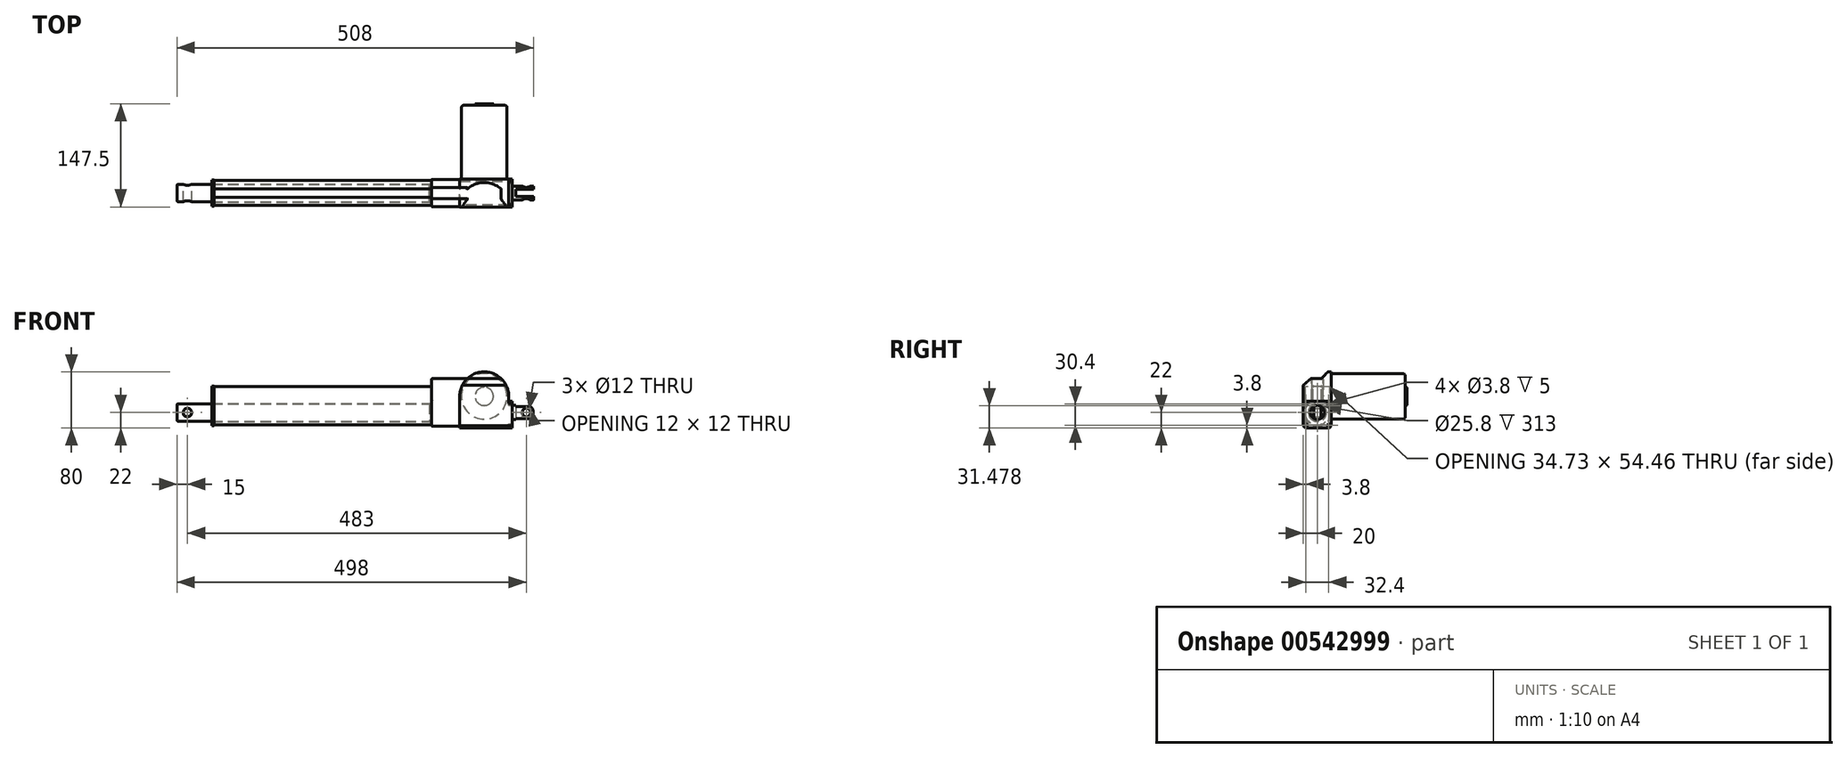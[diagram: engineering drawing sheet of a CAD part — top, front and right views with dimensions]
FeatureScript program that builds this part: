
annotation { "Feature Type Name" : "Feature", "Feature Type Description" : "" }
export const myFeature = defineFeature(function(context is Context, id is Id, definition is map)
    precondition{}
    {
        {
            var Q0;
            Q0=qCreatedBy(makeId("Right.planeOp"),FACE);
            var sketch = newSketch(context, id + "F0", { "sketchPlane" : qUnion([Q0])});
            skCircle(sketch, "E0", {"center": v(0, 0) * mm, "radius": 10 * mm});
            skSolve(sketch);
        }
        {
            var Q0;
            Q0 = qSketchRegion(id + "F0", true);
            var Q1;
            Q1 = qSketchRegion(id + "F2", true);
            extrude(context, id + "F1", {"entities" : qUnion([Q0, Q1]), "depth" : 30 * mm, "offsetDistance" : 25.4 * mm});
        }
        {
            var Q0;
            Q0=qCreatedBy(makeId("Front.planeOp"),FACE);
            var sketch = newSketch(context, id + "F2", { "sketchPlane" : qUnion([Q0])});
            skPoint(sketch, "E1", {"position": v(20, 0) * mm});
            skLineSegment(sketch, "E2", {"start": v(20, -26.83) * mm, "end": v(20, 0) * mm, "construction": true});
            skLineSegment(sketch, "E3", {"start": v(20, 0) * mm, "end": v(20, 12.82) * mm, "construction": true});
            skLineSegment(sketch, "E4", {"start": v(20, 10) * mm, "end": v(30, 10) * mm});
            skLineSegment(sketch, "E5.0", {"start": v(30, 10) * mm, "end": v(30, -10) * mm});
            skLineSegment(sketch, "E6", {"start": v(30, -10) * mm, "end": v(20, -10) * mm});
            skArc(sketch, "E7", {"start": v(20, 10) * mm, "mid": v(30, 0) * mm, "end": v(20, -10) * mm});
            skSolve(sketch);
        }
        {
            var Q0;
            Q0 = qSketchRegion(id + "F2", true);
            extrude(context, id + "F3", {"entities" : qUnion([Q0]), "operationType" : NewBodyOperationType.REMOVE, "oppositeDirection" : true, "depth" : 20 * mm, "offsetDistance" : 25 * mm, "symmetric" : true});
        }
        {
            var Q0;
            Q0=qCreatedBy(makeId("Front.planeOp"),FACE);
            cPlane(context, id + "F4", {"entities" : qUnion([Q0]), "cplaneType" : CPlaneType.OFFSET, "offset" : 20 * mm, "oppositeDirection" : true, "width" : 150 * mm, "height" : 150 * mm});
        }
        {
            var Q0;
            Q0=qCreatedBy(id+"F4.planeOp",FACE);
            var sketch = newSketch(context, id + "F5", { "sketchPlane" : qUnion([Q0])});
            skLineSegment(sketch, "E8", {"start": v(0, 0) * mm, "end": v(20, 0) * mm, "construction": true});
            skCircle(sketch, "E9", {"center": v(20, 0) * mm, "radius": 6 * mm});
            skSolve(sketch);
        }
        {
            var Q0;
            Q0=qCreatedBy(makeId("Right.planeOp"),FACE);
            var sketch = newSketch(context, id + "F6", { "sketchPlane" : qUnion([Q0])});
            skLineSegment(sketch, "E10.bottom", {"start": v(20, 16) * mm, "end": v(-20, 16) * mm});
            skLineSegment(sketch, "E10.top", {"start": v(20, -22) * mm, "end": v(-20, -22) * mm});
            skLineSegment(sketch, "E10.left", {"start": v(20, 16) * mm, "end": v(20, -22) * mm});
            skLineSegment(sketch, "E10.right", {"start": v(-20, 16) * mm, "end": v(-20, -22) * mm});
            skPoint(sketch, "E11.visualSharp", {"position": v(20, 16) * mm});
            skPoint(sketch, "E12.visualSharp", {"position": v(20, -22) * mm});
            skPoint(sketch, "E13.visualSharp", {"position": v(-20, 16) * mm});
            skCircle(sketch, "E14", {"center": v(16.2, 12.2) * mm, "radius": 1.9 * mm});
            skCircle(sketch, "E15", {"center": v(16.2, -18.2) * mm, "radius": 1.9 * mm});
            skCircle(sketch, "E16", {"center": v(-16.2, -18.2) * mm, "radius": 1.9 * mm});
            skCircle(sketch, "E17", {"center": v(-16.2, 12.2) * mm, "radius": 1.9 * mm});
            skSolve(sketch);
        }
        {
            var Q0;
            Q0=makeQuery(id+"F6.imprint","IMPRINT",FACE,{"disambiguationData":[TD([[makeQuery(id+"F6.imprint","IMPRINT",EDGE,{"derivedFrom":sQuery(id+"F6.wireOp",EDGE,"E10.bottom")}),1.0]])]});
            extrude(context, id + "F7", {"entities" : qUnion([Q0]), "operationType" : NewBodyOperationType.ADD, "oppositeDirection" : true, "depth" : 5 * mm, "offsetDistance" : 25 * mm});
        }
        {
            var Q0;
            Q0=qCreatedBy(makeId("Top.planeOp"),FACE);
            cPlane(context, id + "F8", {"entities" : qUnion([Q0]), "cplaneType" : CPlaneType.OFFSET, "offset" : 15 * mm, "oppositeDirection" : true, "width" : 150 * mm, "height" : 150 * mm});
        }
        {
            var Q0;
            Q0=qCreatedBy(id+"F8.planeOp",FACE);
            var sketch = newSketch(context, id + "F9", { "sketchPlane" : qUnion([Q0])});
            skPoint(sketch, "E18.0", {"position": v(30, 0) * mm});
            skLineSegment(sketch, "E19.bottom", {"start": v(30, -5) * mm, "end": v(5, -5) * mm});
            skLineSegment(sketch, "E19.top", {"start": v(30, 5) * mm, "end": v(5, 5) * mm});
            skLineSegment(sketch, "E19.left", {"start": v(30, -5) * mm, "end": v(30, 5) * mm});
            skLineSegment(sketch, "E19.right", {"start": v(5, -5) * mm, "end": v(5, 5) * mm});
            skSolve(sketch);
        }
        {
            var Q0;
            Q0=makeQuery(id+"F9.imprint","IMPRINT",FACE,{"disambiguationData":[TD([[makeQuery(id+"F9.imprint","IMPRINT",EDGE,{"derivedFrom":sQuery(id+"F9.wireOp",EDGE,"E19.bottom")}),-1.0]])]});
            extrude(context, id + "F10", {"entities" : qUnion([Q0]), "operationType" : NewBodyOperationType.REMOVE, "endBound" : BoundingType.THROUGH_ALL, "depth" : 26.4 * mm, "offsetDistance" : 25 * mm});
        }
        {
            var Q0;
            Q0=makeQuery(id+"F7.opExtrude","SWEPT_EDGE",EDGE,{"disambiguationData":[OSD([sQuery(id+"F6.wireOp",EDGE,"E10.top"),sQuery(id+"F6.wireOp",EDGE,"E10.left")])]});
            var Q1;
            Q1=makeQuery(id+"F7.opExtrude","SWEPT_EDGE",EDGE,{"disambiguationData":[OSD([sQuery(id+"F6.wireOp",EDGE,"E10.bottom"),sQuery(id+"F6.wireOp",EDGE,"E10.left")])]});
            var Q2;
            Q2=makeQuery(id+"F7.opExtrude","SWEPT_EDGE",EDGE,{"disambiguationData":[OSD([sQuery(id+"F6.wireOp",EDGE,"E10.bottom"),sQuery(id+"F6.wireOp",EDGE,"E10.right")])]});
            var Q3;
            Q3=makeQuery(id+"F7.opExtrude","SWEPT_EDGE",EDGE,{"disambiguationData":[OSD([sQuery(id+"F6.wireOp",EDGE,"E10.top"),sQuery(id+"F6.wireOp",EDGE,"E10.right")])]});
            chamfer(context, id + "F11", {"entities" : qUnion([Q0, Q1, Q2, Q3]), "width" : 3 * mm, "tangentPropagation" : true});
        }
        {
            var Q0;
            Q0=qCreatedBy(id+"F4.planeOp",FACE);
            var sketch = newSketch(context, id + "F12", { "sketchPlane" : qUnion([Q0])});
            skPoint(sketch, "E20.0", {"position": v(0, -22) * mm});
            skLineSegment(sketch, "E21.0", {"start": v(-5, 13) * mm, "end": v(-5, -19) * mm});
            skLineSegment(sketch, "E22", {"start": v(-5, -19) * mm, "end": v(-5, -22) * mm, "construction": true});
            skLineSegment(sketch, "E23", {"start": v(-5, -22) * mm, "end": v(-65.97, -22) * mm, "construction": true});
            skLineSegment(sketch, "E24.bottom", {"start": v(-5, -22) * mm, "end": v(-75, -22) * mm});
            skLineSegment(sketch, "E24.top", {"start": v(-5, 58) * mm, "end": v(-75, 58) * mm});
            skLineSegment(sketch, "E24.left", {"start": v(-5, -22) * mm, "end": v(-5, 58) * mm});
            skLineSegment(sketch, "E24.right", {"start": v(-75, -22) * mm, "end": v(-75, 58) * mm});
            skLineSegment(sketch, "E25", {"start": v(-40, 58) * mm, "end": v(-40, -22) * mm, "construction": true});
            skLineSegment(sketch, "E26.0", {"start": v(-5, 25.5) * mm, "end": v(-75, 25.5) * mm, "construction": true});
            skSolve(sketch);
        }
        {
            var Q0;
            {var subQ0=sQuery(id+"F12.wireOp",EDGE,"E24.bottom");Q0=makeQuery(id+"F12.imprint","IMPRINT",FACE,{"disambiguationData":[TD([[makeQuery(id+"F12.imprint","IMPRINT",EDGE,{"derivedFrom":subQ0}),-1.0]])]});}
            extrude(context, id + "F13", {"entities" : qUnion([Q0]), "operationType" : NewBodyOperationType.ADD, "depth" : 40 * mm, "offsetDistance" : 25 * mm});
        }
        {
            var Q0;
            Q0=makeQuery(id+"F13.opExtrude","CAP_EDGE",EDGE,{"disambiguationData":[OSD([sQuery(id+"F12.wireOp",EDGE,"E24.bottom")])],"isStart":false});
            var Q1;
            Q1=makeQuery(id+"F13.opExtrude","CAP_EDGE",EDGE,{"disambiguationData":[OSD([sQuery(id+"F12.wireOp",EDGE,"E24.bottom")])],"isStart":true});
            chamfer(context, id + "F14", {"entities" : qUnion([Q0, Q1]), "width" : 3 * mm, "tangentPropagation" : true});
        }
        {
            var Q0;
            Q0=qCreatedBy(id+"F4.planeOp",FACE);
            var sketch = newSketch(context, id + "F15", { "sketchPlane" : qUnion([Q0])});
            skLineSegment(sketch, "E27.0", {"start": v(10.95, 23) * mm, "end": v(-90.95, 23) * mm, "construction": true});
            skLineSegment(sketch, "E28.0", {"start": v(-5, 58) * mm, "end": v(-75, 58) * mm});
            skLineSegment(sketch, "E29", {"start": v(-40, 58) * mm, "end": v(-40, -15.27) * mm, "construction": true});
            skCircle(sketch, "E30", {"center": v(-40, 23) * mm, "radius": 32.5 * mm});
            skLineSegment(sketch, "E31.0", {"start": v(-5, 13) * mm, "end": v(-5, 58) * mm});
            skLineSegment(sketch, "E32.0", {"start": v(-75, -19) * mm, "end": v(-75, 58) * mm});
            skPoint(sketch, "E33", {"position": v(-75, 23) * mm});
            skPoint(sketch, "E34", {"position": v(-5, 23) * mm});
            skArc(sketch, "E35", {"start": v(-5, 23) * mm, "mid": v(-40, 58) * mm, "end": v(-75, 23) * mm});
            skSolve(sketch);
        }
        {
            var Q0;
            Q0=makeQuery(id+"F15.imprint","IMPRINT",FACE,{"disambiguationData":[TD([[makeQuery(id+"F15.imprint","IMPRINT",EDGE,{"derivedFrom":sQuery(id+"F15.wireOp",EDGE,"E30")}),1.0]])]});
            extrude(context, id + "F16", {"entities" : qUnion([Q0]), "operationType" : NewBodyOperationType.ADD, "oppositeDirection" : true, "depth" : 105 * mm, "offsetDistance" : 25 * mm});
        }
        {
            var Q0;
            Q0=makeQuery(id+"F16.opExtrude","CAP_EDGE",EDGE,{"disambiguationData":[OSD([sQuery(id+"F15.wireOp",EDGE,"E30")])],"isStart":false});
            fillet(context, id + "F17", {"entities" : qUnion([Q0]), "radius" : 3 * mm, "tangentPropagation" : true, "allowEdgeOverflow" : false});
        }
        {
            var Q0;
            Q0=makeQuery(id+"F16.opExtrude","CAP_FACE",FACE,{"disambiguationData":[OSD([sQuery(id+"F15.wireOp",EDGE,"E30")])],"isStart":false});
            var sketch = newSketch(context, id + "F18", { "sketchPlane" : qUnion([Q0])});
            skCircle(sketch, "E36", {"center": v(40, 23) * mm, "radius": 13.03 * mm});
            skSolve(sketch);
        }
        {
            var Q0;
            Q0=makeQuery(id+"F18.imprint","IMPRINT",FACE,{"disambiguationData":[TD([[makeQuery(id+"F18.imprint","IMPRINT",EDGE,{"derivedFrom":sQuery(id+"F18.wireOp",EDGE,"E36")}),1.0]])]});
            extrude(context, id + "F19", {"entities" : qUnion([Q0]), "operationType" : NewBodyOperationType.ADD, "depth" : 2.5 * mm, "offsetDistance" : 25 * mm});
        }
        {
            var Q0;
            Q0=makeQuery(id+"F19.opExtrude","CAP_EDGE",EDGE,{"disambiguationData":[OSD([sQuery(id+"F18.wireOp",EDGE,"E36")])],"isStart":false});
            var Q1;
            Q1=makeQuery(id+"F19.opExtrude","CAP_EDGE",EDGE,{"disambiguationData":[OSD([sQuery(id+"F18.wireOp",EDGE,"E36")])],"isStart":true});
            fillet(context, id + "F20", {"entities" : qUnion([Q0, Q1]), "radius" : 1 * mm, "tangentPropagation" : true, "allowEdgeOverflow" : false});
        }
        {
            var Q0;
            {var subQ0=sQuery(id+"F15.wireOp",EDGE,"E31.0");var subQ1=sQuery(id+"F15.wireOp",EDGE,"E28.0");var subQ2=makeQuery(id+"F15.imprint","INTERSECT",VERTEX,{"derivedFrom":[subQ1,subQ0]});Q0=makeQuery(id+"F15.imprint","IMPRINT",FACE,{"disambiguationData":[TD([[makeQuery(id+"F15.imprint","IMPRINT",EDGE,{"disambiguationData":[TD([[subQ2,-1.0]])],"derivedFrom":subQ1}),1.0]])]});}
            var Q1;
            {var subQ0=sQuery(id+"F15.wireOp",EDGE,"E32.0");var subQ1=sQuery(id+"F15.wireOp",EDGE,"E28.0");var subQ2=makeQuery(id+"F15.imprint","INTERSECT",VERTEX,{"derivedFrom":[subQ1,subQ0]});Q1=makeQuery(id+"F15.imprint","IMPRINT",FACE,{"disambiguationData":[TD([[makeQuery(id+"F15.imprint","IMPRINT",EDGE,{"disambiguationData":[TD([[subQ2,1.0]])],"derivedFrom":subQ1}),1.0]])]});}
            extrude(context, id + "F21", {"entities" : qUnion([Q0, Q1]), "operationType" : NewBodyOperationType.REMOVE, "endBound" : BoundingType.THROUGH_ALL, "depth" : 54.8 * mm, "offsetDistance" : 25 * mm});
        }
        {
            var Q0;
            Q0=qCreatedBy(makeId("Right.planeOp"),FACE);
            var sketch = newSketch(context, id + "F22", { "sketchPlane" : qUnion([Q0])});
            skLineSegment(sketch, "E37", {"start": v(-20, 58) * mm, "end": v(20, 58) * mm});
            skPoint(sketch, "E38.0", {"position": v(-20, 16) * mm});
            skLineSegment(sketch, "E38.1", {"start": v(20, 16) * mm, "end": v(-20, 16) * mm});
            skPoint(sketch, "E38.2", {"position": v(20, 16) * mm});
            skLineSegment(sketch, "E39", {"start": v(-20, 38.83) * mm, "end": v(-9.23, 48.31) * mm});
            skLineSegment(sketch, "E40", {"start": v(-9.23, 48.31) * mm, "end": v(5.89, 48.31) * mm});
            skLineSegment(sketch, "E41", {"start": v(5.89, 48.31) * mm, "end": v(14.95, 58) * mm});
            skLineSegment(sketch, "E42", {"start": v(-20, 58) * mm, "end": v(-20, 16) * mm});
            skSolve(sketch);
        }
        {
            var Q0;
            {var subQ1=sQuery(id+"F22.wireOp",EDGE,"E39");Q0=makeQuery(id+"F22.imprint","IMPRINT",FACE,{"disambiguationData":[TD([[makeQuery(id+"F22.imprint","IMPRINT",EDGE,{"derivedFrom":subQ1}),1.0]])]});}
            extrude(context, id + "F23", {"entities" : qUnion([Q0]), "operationType" : NewBodyOperationType.REMOVE, "endBound" : BoundingType.THROUGH_ALL, "oppositeDirection" : true, "depth" : 25 * mm, "offsetDistance" : 25 * mm});
        }
        {
            var Q0;
            {var subQ0=sQuery(id+"F15.wireOp",EDGE,"E35");Q0=makeQuery(id+"F23.boolean.opBoolean","INTERSECT",EDGE,{"derivedFrom":[makeQuery(id+"F21.boolean.opBoolean","TWEAK_FACE",FACE,{"derivedFrom":[makeQuery(id+"F21.opExtrude","SWEPT_FACE",FACE,{"disambiguationData":[OSD([subQ0]),TDD([makeQuery(id+"F15.imprint","IMPRINT",EDGE,{"disambiguationData":[TD([[makeQuery(id+"F15.imprint","INTERSECT",VERTEX,{"derivedFrom":[sQuery(id+"F15.wireOp",EDGE,"E31.0"),subQ0]}),-1.0]])],"derivedFrom":subQ0})])]}),makeQuery(id+"F21.opExtrude","SWEPT_FACE",FACE,{"disambiguationData":[OSD([subQ0]),TDD([makeQuery(id+"F15.imprint","IMPRINT",EDGE,{"disambiguationData":[TD([[makeQuery(id+"F15.imprint","INTERSECT",VERTEX,{"derivedFrom":[sQuery(id+"F15.wireOp",EDGE,"E32.0"),subQ0]}),1.0]])],"derivedFrom":subQ0})])]})]}),makeQuery(id+"F23.opExtrude","SWEPT_FACE",FACE,{"disambiguationData":[OSD([sQuery(id+"F22.wireOp",EDGE,"E41")])]})]});}
            var Q1;
            Q1=makeQuery(id+"F23.boolean.opBoolean","COPY",EDGE,{"derivedFrom":makeQuery(id+"F23.opExtrude","SWEPT_EDGE",EDGE,{"disambiguationData":[OSD([sQuery(id+"F22.wireOp",EDGE,"E40"),sQuery(id+"F22.wireOp",EDGE,"E41")])]})});
            var Q2;
            {var subQ0=sQuery(id+"F15.wireOp",EDGE,"E35");Q2=makeQuery(id+"F23.boolean.opBoolean","INTERSECT",EDGE,{"disambiguationData":[OD(1.0)],"derivedFrom":[makeQuery(id+"F21.boolean.opBoolean","TWEAK_FACE",FACE,{"derivedFrom":[makeQuery(id+"F21.opExtrude","SWEPT_FACE",FACE,{"disambiguationData":[OSD([subQ0]),TDD([makeQuery(id+"F15.imprint","IMPRINT",EDGE,{"disambiguationData":[TD([[makeQuery(id+"F15.imprint","INTERSECT",VERTEX,{"derivedFrom":[sQuery(id+"F15.wireOp",EDGE,"E31.0"),subQ0]}),-1.0]])],"derivedFrom":subQ0})])]}),makeQuery(id+"F21.opExtrude","SWEPT_FACE",FACE,{"disambiguationData":[OSD([subQ0]),TDD([makeQuery(id+"F15.imprint","IMPRINT",EDGE,{"disambiguationData":[TD([[makeQuery(id+"F15.imprint","INTERSECT",VERTEX,{"derivedFrom":[sQuery(id+"F15.wireOp",EDGE,"E32.0"),subQ0]}),1.0]])],"derivedFrom":subQ0})])]})]}),makeQuery(id+"F23.opExtrude","SWEPT_FACE",FACE,{"disambiguationData":[OSD([sQuery(id+"F22.wireOp",EDGE,"E40")])]})]});}
            var Q3;
            {var subQ0=sQuery(id+"F15.wireOp",EDGE,"E35");Q3=makeQuery(id+"F23.boolean.opBoolean","INTERSECT",EDGE,{"disambiguationData":[OD(0.0)],"derivedFrom":[makeQuery(id+"F21.boolean.opBoolean","TWEAK_FACE",FACE,{"derivedFrom":[makeQuery(id+"F21.opExtrude","SWEPT_FACE",FACE,{"disambiguationData":[OSD([subQ0]),TDD([makeQuery(id+"F15.imprint","IMPRINT",EDGE,{"disambiguationData":[TD([[makeQuery(id+"F15.imprint","INTERSECT",VERTEX,{"derivedFrom":[sQuery(id+"F15.wireOp",EDGE,"E31.0"),subQ0]}),-1.0]])],"derivedFrom":subQ0})])]}),makeQuery(id+"F21.opExtrude","SWEPT_FACE",FACE,{"disambiguationData":[OSD([subQ0]),TDD([makeQuery(id+"F15.imprint","IMPRINT",EDGE,{"disambiguationData":[TD([[makeQuery(id+"F15.imprint","INTERSECT",VERTEX,{"derivedFrom":[sQuery(id+"F15.wireOp",EDGE,"E32.0"),subQ0]}),1.0]])],"derivedFrom":subQ0})])]})]}),makeQuery(id+"F23.opExtrude","SWEPT_FACE",FACE,{"disambiguationData":[OSD([sQuery(id+"F22.wireOp",EDGE,"E40")])]})]});}
            var Q4;
            Q4=makeQuery(id+"F23.boolean.opBoolean","COPY",EDGE,{"derivedFrom":makeQuery(id+"F23.opExtrude","SWEPT_EDGE",EDGE,{"disambiguationData":[OSD([sQuery(id+"F22.wireOp",EDGE,"E39"),sQuery(id+"F22.wireOp",EDGE,"E40")])]})});
            var Q5;
            {var subQ0=sQuery(id+"F15.wireOp",EDGE,"E35");Q5=makeQuery(id+"F23.boolean.opBoolean","INTERSECT",EDGE,{"disambiguationData":[OD(1.0)],"derivedFrom":[makeQuery(id+"F21.boolean.opBoolean","TWEAK_FACE",FACE,{"derivedFrom":[makeQuery(id+"F21.opExtrude","SWEPT_FACE",FACE,{"disambiguationData":[OSD([subQ0]),TDD([makeQuery(id+"F15.imprint","IMPRINT",EDGE,{"disambiguationData":[TD([[makeQuery(id+"F15.imprint","INTERSECT",VERTEX,{"derivedFrom":[sQuery(id+"F15.wireOp",EDGE,"E31.0"),subQ0]}),-1.0]])],"derivedFrom":subQ0})])]}),makeQuery(id+"F21.opExtrude","SWEPT_FACE",FACE,{"disambiguationData":[OSD([subQ0]),TDD([makeQuery(id+"F15.imprint","IMPRINT",EDGE,{"disambiguationData":[TD([[makeQuery(id+"F15.imprint","INTERSECT",VERTEX,{"derivedFrom":[sQuery(id+"F15.wireOp",EDGE,"E32.0"),subQ0]}),1.0]])],"derivedFrom":subQ0})])]})]}),makeQuery(id+"F23.opExtrude","SWEPT_FACE",FACE,{"disambiguationData":[OSD([sQuery(id+"F22.wireOp",EDGE,"E39")])]})]});}
            var Q6;
            {var subQ0=sQuery(id+"F15.wireOp",EDGE,"E35");Q6=makeQuery(id+"F23.boolean.opBoolean","INTERSECT",EDGE,{"disambiguationData":[OD(0.0)],"derivedFrom":[makeQuery(id+"F21.boolean.opBoolean","TWEAK_FACE",FACE,{"derivedFrom":[makeQuery(id+"F21.opExtrude","SWEPT_FACE",FACE,{"disambiguationData":[OSD([subQ0]),TDD([makeQuery(id+"F15.imprint","IMPRINT",EDGE,{"disambiguationData":[TD([[makeQuery(id+"F15.imprint","INTERSECT",VERTEX,{"derivedFrom":[sQuery(id+"F15.wireOp",EDGE,"E31.0"),subQ0]}),-1.0]])],"derivedFrom":subQ0})])]}),makeQuery(id+"F21.opExtrude","SWEPT_FACE",FACE,{"disambiguationData":[OSD([subQ0]),TDD([makeQuery(id+"F15.imprint","IMPRINT",EDGE,{"disambiguationData":[TD([[makeQuery(id+"F15.imprint","INTERSECT",VERTEX,{"derivedFrom":[sQuery(id+"F15.wireOp",EDGE,"E32.0"),subQ0]}),1.0]])],"derivedFrom":subQ0})])]})]}),makeQuery(id+"F23.opExtrude","SWEPT_FACE",FACE,{"disambiguationData":[OSD([sQuery(id+"F22.wireOp",EDGE,"E39")])]})]});}
            var Q7;
            Q7=makeQuery(id+"F23.boolean.opBoolean","COPY",EDGE,{"derivedFrom":makeQuery(id+"F23.opExtrude","SWEPT_EDGE",EDGE,{"disambiguationData":[OSD([sQuery(id+"F22.wireOp",EDGE,"E39"),sQuery(id+"F22.wireOp",EDGE,"E42")])]})});
            fillet(context, id + "F24", {"entities" : qUnion([Q0, Q1, Q2, Q3, Q4, Q5, Q6, Q7]), "radius" : 2.5 * mm, "tangentPropagation" : true, "allowEdgeOverflow" : false});
        }
        {
            var Q0;
            Q0=makeQuery(id+"F13.opExtrude","SWEPT_FACE",FACE,{"disambiguationData":[OSD([sQuery(id+"F12.wireOp",EDGE,"E24.right")])]});
            cPlane(context, id + "F25", {"entities" : qUnion([Q0]), "cplaneType" : CPlaneType.OFFSET, "offset" : 0 * mm, "width" : 150 * mm, "height" : 150 * mm});
        }
        {
            var Q0;
            Q0=qCreatedBy(id+"F25.planeOp",FACE);
            var sketch = newSketch(context, id + "F26", { "sketchPlane" : qUnion([Q0])});
            skPoint(sketch, "E43.0", {"position": v(0, 0) * mm});
            skCircle(sketch, "E44", {"center": v(0, 0) * mm, "radius": 19.5 * mm});
            skLineSegment(sketch, "E45", {"start": v(0, 0) * mm, "end": v(0, 41.64) * mm, "construction": true});
            skLineSegment(sketch, "E46.0", {"start": v(8, 17.78) * mm, "end": v(8, 48.31) * mm});
            skLineSegment(sketch, "E47.0", {"start": v(-8, 17.78) * mm, "end": v(-8, 48.31) * mm});
            skLineSegment(sketch, "E48", {"start": v(8, 48.31) * mm, "end": v(-8, 48.31) * mm});
            skSolve(sketch);
        }
        {
            var Q0;
            {var subQ0=sQuery(id+"F26.wireOp",EDGE,"E44");var subQ1=makeQuery(id+"F26.imprint","INTERSECT",VERTEX,{"derivedFrom":[subQ0,sQuery(id+"F26.wireOp",EDGE,"E46.0")]});Q0=makeQuery(id+"F26.imprint","IMPRINT",FACE,{"disambiguationData":[TD([[makeQuery(id+"F26.imprint","IMPRINT",EDGE,{"disambiguationData":[TD([[subQ1,-1.0]])],"derivedFrom":subQ0}),1.0]])]});}
            var Q1;
            {var subQ0=sQuery(id+"F26.wireOp",EDGE,"E46.0");Q1=makeQuery(id+"F26.imprint","IMPRINT",FACE,{"disambiguationData":[TD([[makeQuery(id+"F26.imprint","IMPRINT",EDGE,{"derivedFrom":subQ0}),1.0]])]});}
            extrude(context, id + "F27", {"entities" : qUnion([Q0, Q1]), "operationType" : NewBodyOperationType.ADD, "depth" : 40 * mm, "offsetDistance" : 25 * mm});
        }
        {
            var Q0;
            Q0=makeQuery(id+"F27.opExtrude","CAP_FACE",FACE,{"disambiguationData":[OSD([sQuery(id+"F26.wireOp",EDGE,"E44"),sQuery(id+"F26.wireOp",EDGE,"E46.0"),sQuery(id+"F26.wireOp",EDGE,"E47.0"),sQuery(id+"F26.wireOp",EDGE,"E48")])],"isStart":true});
            extrude(context, id + "F28", {"entities" : qUnion([Q0]), "operationType" : NewBodyOperationType.ADD, "endBound" : BoundingType.UP_TO_NEXT, "depth" : 25 * mm, "offsetDistance" : 25 * mm});
        }
        {
            var Q0;
            {var subQ0=sQuery(id+"F26.wireOp",EDGE,"E48");var subQ1=sQuery(id+"F26.wireOp",EDGE,"E46.0");Q0=makeQuery(id+"F28.boolean.opBoolean","MERGE",EDGE,{"derivedFrom":[makeQuery(id+"F27.opExtrude","SWEPT_EDGE",EDGE,{"disambiguationData":[OSD([subQ1,subQ0])]}),makeQuery(id+"F28.opExtrude","SWEPT_EDGE",EDGE,{"disambiguationData":[OSD([subQ1,subQ0])]})]});}
            var Q1;
            Q1=makeQuery(id+"F27.opExtrude","SWEPT_EDGE",EDGE,{"disambiguationData":[OSD([sQuery(id+"F26.wireOp",EDGE,"E44"),sQuery(id+"F26.wireOp",EDGE,"E46.0")])]});
            var Q2;
            {var subQ0=sQuery(id+"F26.wireOp",EDGE,"E48");var subQ1=sQuery(id+"F26.wireOp",EDGE,"E47.0");Q2=makeQuery(id+"F28.boolean.opBoolean","MERGE",EDGE,{"derivedFrom":[makeQuery(id+"F27.opExtrude","SWEPT_EDGE",EDGE,{"disambiguationData":[OSD([subQ1,subQ0])]}),makeQuery(id+"F28.opExtrude","SWEPT_EDGE",EDGE,{"disambiguationData":[OSD([subQ1,subQ0])]})]});}
            var Q3;
            Q3=makeQuery(id+"F27.opExtrude","SWEPT_EDGE",EDGE,{"disambiguationData":[OSD([sQuery(id+"F26.wireOp",EDGE,"E44"),sQuery(id+"F26.wireOp",EDGE,"E47.0")])]});
            var Q4;
            Q4=makeQuery(id+"F27.opExtrude","CAP_EDGE",EDGE,{"disambiguationData":[OSD([sQuery(id+"F26.wireOp",EDGE,"E46.0")])],"isStart":false});
            var Q5;
            Q5=makeQuery(id+"F27.opExtrude","CAP_EDGE",EDGE,{"disambiguationData":[OSD([sQuery(id+"F26.wireOp",EDGE,"E48")])],"isStart":false});
            fillet(context, id + "F29", {"entities" : qUnion([Q0, Q1, Q2, Q3, Q4, Q5]), "radius" : 1 * mm, "tangentPropagation" : true, "allowEdgeOverflow" : false});
        }
        {
            var Q0;
            Q0=makeQuery(id+"F27.opExtrude","CAP_FACE",FACE,{"disambiguationData":[OSD([sQuery(id+"F26.wireOp",EDGE,"E44"),sQuery(id+"F26.wireOp",EDGE,"E46.0"),sQuery(id+"F26.wireOp",EDGE,"E47.0"),sQuery(id+"F26.wireOp",EDGE,"E48")])],"isStart":false});
            cPlane(context, id + "F30", {"entities" : qUnion([Q0]), "cplaneType" : CPlaneType.OFFSET, "offset" : 0 * mm, "width" : 150 * mm, "height" : 150 * mm});
        }
        {
            var Q0;
            Q0=qCreatedBy(id+"F30.planeOp",FACE);
            var sketch = newSketch(context, id + "F31", { "sketchPlane" : qUnion([Q0])});
            skPoint(sketch, "E49.0", {"position": v(0, 0) * mm});
            skLineSegment(sketch, "E50", {"start": v(0, 0) * mm, "end": v(0, 35.64) * mm, "construction": true});
            skLineSegment(sketch, "E51.0", {"start": v(6, 18.06) * mm, "end": v(6, 35.7) * mm});
            skLineSegment(sketch, "E52.0", {"start": v(-6, 18.06) * mm, "end": v(-6, 35.7) * mm});
            skLineSegment(sketch, "E53", {"start": v(-5, 36.7) * mm, "end": v(5, 36.7) * mm});
            skPoint(sketch, "E54.visualSharp", {"position": v(-6, 36.7) * mm});
            skArc(sketch, "E54.filletArc", {"start": v(-5, 36.7) * mm, "mid": v(-5.7, 36.41) * mm, "end": v(-6, 35.7) * mm});
            skPoint(sketch, "E55.visualSharp", {"position": v(6, 36.7) * mm});
            skArc(sketch, "E55.filletArc", {"start": v(6, 35.7) * mm, "mid": v(5.7, 36.41) * mm, "end": v(5, 36.7) * mm});
            skArc(sketch, "E56", {"start": v(7.19, 16.23) * mm, "mid": v(0, -17.75) * mm, "end": v(-7.19, 16.23) * mm});
            skPoint(sketch, "E57.visualSharp", {"position": v(-6, 16.7) * mm});
            skArc(sketch, "E57.filletArc", {"start": v(-7.19, 16.23) * mm, "mid": v(-6.32, 16.97) * mm, "end": v(-6, 18.06) * mm});
            skPoint(sketch, "E58.visualSharp", {"position": v(6, 16.7) * mm});
            skArc(sketch, "E58.filletArc", {"start": v(6, 18.06) * mm, "mid": v(6.32, 16.97) * mm, "end": v(7.19, 16.23) * mm});
            skCircle(sketch, "E59", {"center": v(0, 0) * mm, "radius": 12.9 * mm});
            skSolve(sketch);
        }
        {
            var Q0;
            Q0=makeQuery(id+"F31.imprint","IMPRINT",FACE,{"disambiguationData":[TD([[makeQuery(id+"F31.imprint","IMPRINT",EDGE,{"derivedFrom":sQuery(id+"F31.wireOp",EDGE,"E51.0")}),1.0]])]});
            extrude(context, id + "F32", {"entities" : qUnion([Q0]), "operationType" : NewBodyOperationType.ADD, "depth" : 310 * mm, "offsetDistance" : 25 * mm});
        }
        {
            var Q0;
            Q0=makeQuery(id+"F32.opExtrude","CAP_FACE",FACE,{"disambiguationData":[OSD([sQuery(id+"F31.wireOp",EDGE,"87hEAqkd-yjAr-Z6zJ-uZvU-nRcljvAD9QsZ"),sQuery(id+"F31.wireOp",EDGE,"E51.0"),sQuery(id+"F31.wireOp",EDGE,"E52.0"),sQuery(id+"F31.wireOp",EDGE,"E53")])],"isStart":false});
            cPlane(context, id + "F33", {"entities" : qUnion([Q0]), "cplaneType" : CPlaneType.OFFSET, "offset" : 0 * mm, "width" : 150 * mm, "height" : 150 * mm});
        }
        {
            var Q0;
            Q0=qCreatedBy(id+"F33.planeOp",FACE);
            var sketch = newSketch(context, id + "F34", { "sketchPlane" : qUnion([Q0])});
            skArc(sketch, "E60.0", {"start": v(-8.13, 16.9) * mm, "mid": v(0, -18.75) * mm, "end": v(8.13, 16.9) * mm});
            skLineSegment(sketch, "E60.1", {"start": v(-7, 35.7) * mm, "end": v(-7, 18.7) * mm});
            skLineSegment(sketch, "E60.2", {"start": v(5, 37.7) * mm, "end": v(-5, 37.7) * mm});
            skLineSegment(sketch, "E60.3", {"start": v(7, 18.7) * mm, "end": v(7, 35.7) * mm});
            skPoint(sketch, "E61.visualSharp", {"position": v(-7, 37.7) * mm});
            skArc(sketch, "E61.filletArc", {"start": v(-5, 37.7) * mm, "mid": v(-6.41, 37.12) * mm, "end": v(-7, 35.7) * mm});
            skPoint(sketch, "E62.visualSharp", {"position": v(7, 37.7) * mm});
            skArc(sketch, "E62.filletArc", {"start": v(7, 35.7) * mm, "mid": v(6.41, 37.12) * mm, "end": v(5, 37.7) * mm});
            skPoint(sketch, "E63.visualSharp", {"position": v(-7, 17.4) * mm});
            skArc(sketch, "E63.filletArc", {"start": v(-8.13, 16.9) * mm, "mid": v(-7.3, 17.63) * mm, "end": v(-7, 18.7) * mm});
            skPoint(sketch, "E64.visualSharp", {"position": v(7, 17.4) * mm});
            skArc(sketch, "E64.filletArc", {"start": v(7, 18.7) * mm, "mid": v(7.3, 17.63) * mm, "end": v(8.13, 16.9) * mm});
            skCircle(sketch, "E65.0", {"center": v(0, 0) * mm, "radius": 12.9 * mm});
            skLineSegment(sketch, "E66", {"start": v(0, 37.7) * mm, "end": v(0, -24.37) * mm, "construction": true});
            skPoint(sketch, "E66.endSnap0", {"position": v(0, -18.75) * mm});
            skSolve(sketch);
        }
        {
            var Q0;
            Q0=makeQuery(id+"F34.imprint","IMPRINT",FACE,{"disambiguationData":[TD([[makeQuery(id+"F34.imprint","IMPRINT",EDGE,{"derivedFrom":sQuery(id+"F34.wireOp",EDGE,"E60.0")}),1.0]])]});
            extrude(context, id + "F35", {"entities" : qUnion([Q0]), "operationType" : NewBodyOperationType.ADD, "depth" : 3 * mm, "offsetDistance" : 25 * mm});
        }
        {
            var Q0;
            Q0=makeQuery(id+"F35.opExtrude","CAP_FACE",FACE,{"disambiguationData":[OSD([sQuery(id+"F34.wireOp",EDGE,"E60.0"),sQuery(id+"F34.wireOp",EDGE,"E60.1"),sQuery(id+"F34.wireOp",EDGE,"E60.2"),sQuery(id+"F34.wireOp",EDGE,"E60.3"),sQuery(id+"F34.wireOp",EDGE,"E61.filletArc"),sQuery(id+"F34.wireOp",EDGE,"E62.filletArc"),sQuery(id+"F34.wireOp",EDGE,"E63.filletArc"),sQuery(id+"F34.wireOp",EDGE,"E64.filletArc")])],"isStart":false});
            cPlane(context, id + "F36", {"entities" : qUnion([Q0]), "cplaneType" : CPlaneType.OFFSET, "offset" : 0 * mm, "width" : 150 * mm, "height" : 150 * mm});
        }
        {
            var Q0;
            Q0=qCreatedBy(id+"F36.planeOp",FACE);
            var sketch = newSketch(context, id + "F37", { "sketchPlane" : qUnion([Q0])});
            skPoint(sketch, "E67.0", {"position": v(0, 0) * mm});
            skCircle(sketch, "E68", {"center": v(0, 0) * mm, "radius": 12.5 * mm});
            skSolve(sketch);
        }
        {
            var Q0;
            Q0=makeQuery(id+"F37.imprint","IMPRINT",FACE,{"disambiguationData":[TD([[makeQuery(id+"F37.imprint","IMPRINT",EDGE,{"derivedFrom":sQuery(id+"F37.wireOp",EDGE,"E68")}),1.0]])]});
            extrude(context, id + "F38", {"entities" : qUnion([Q0]), "operationType" : NewBodyOperationType.ADD, "depth" : 50 * mm, "offsetDistance" : 25 * mm});
        }
        {
            var Q0;
            Q0=makeQuery(id+"F38.opExtrude","CAP_FACE",FACE,{"disambiguationData":[OSD([sQuery(id+"F37.wireOp",EDGE,"E68")])],"isStart":false});
            fillet(context, id + "F39", {"entities" : qUnion([Q0]), "radius" : 2 * mm, "tangentPropagation" : true, "allowEdgeOverflow" : false});
        }
        {
            var Q0;
            Q0=qCreatedBy(id+"F4.planeOp",FACE);
            var sketch = newSketch(context, id + "F40", { "sketchPlane" : qUnion([Q0])});
            skLineSegment(sketch, "E69", {"start": v(-478, -10.5) * mm, "end": v(-478, 10.5) * mm, "construction": true});
            skLineSegment(sketch, "E70.0", {"start": v(-463, -10.5) * mm, "end": v(-463, 10.5) * mm, "construction": true});
            skCircle(sketch, "E71", {"center": v(-463, 0) * mm, "radius": 6 * mm});
            skSolve(sketch);
        }
        {
            var Q0;
            Q0=makeQuery(id+"F5.imprint","IMPRINT",FACE,{"disambiguationData":[TD([[makeQuery(id+"F5.imprint","IMPRINT",EDGE,{"derivedFrom":sQuery(id+"F5.wireOp",EDGE,"E9")}),1.0]])]});
            extrude(context, id + "F41", {"entities" : qUnion([Q0]), "operationType" : NewBodyOperationType.REMOVE, "endBound" : BoundingType.THROUGH_ALL, "depth" : 18.4 * mm, "offsetDistance" : 25 * mm});
        }
        {
            var Q0;
            Q0 = qSketchRegion(id + "F37", true);
            extrude(context, id + "F42", {"entities" : qUnion([Q0]), "operationType" : NewBodyOperationType.ADD, "oppositeDirection" : true, "depth" : 310 * mm, "offsetDistance" : 25 * mm});
        }
        {
            var Q0;
            Q0=makeQuery(id+"F40.imprint","IMPRINT",FACE,{"disambiguationData":[TD([[makeQuery(id+"F40.imprint","IMPRINT",EDGE,{"derivedFrom":sQuery(id+"F40.wireOp",EDGE,"E71")}),1.0]])]});
            extrude(context, id + "F43", {"entities" : qUnion([Q0]), "operationType" : NewBodyOperationType.REMOVE, "endBound" : BoundingType.THROUGH_ALL, "depth" : 16 * mm, "offsetDistance" : 25 * mm});
        }
    });
